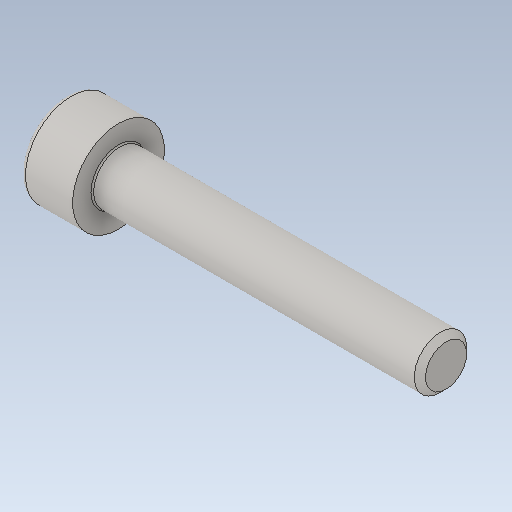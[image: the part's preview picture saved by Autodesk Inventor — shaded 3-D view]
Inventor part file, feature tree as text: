
AUTODESK INVENTOR PART (.ipt)
format: ipt  version: 2020.2 (Build 242310000, 310)  size: 131,584 bytes
history: imported  units: mm
features: imported_body x1
ambient origin geometry x8: Origin, YZ Plane, XZ Plane, XY Plane, X Axis, Y Axis, Z Axis, Center Point
bodies: Solide1 (imported_parasolid), Solid1 (imported_parasolid)
feature tree (1):
  imported_body  NMx_Import_Brep_tag  [imported B-rep: ~5 faces, bbox_mm=None]
